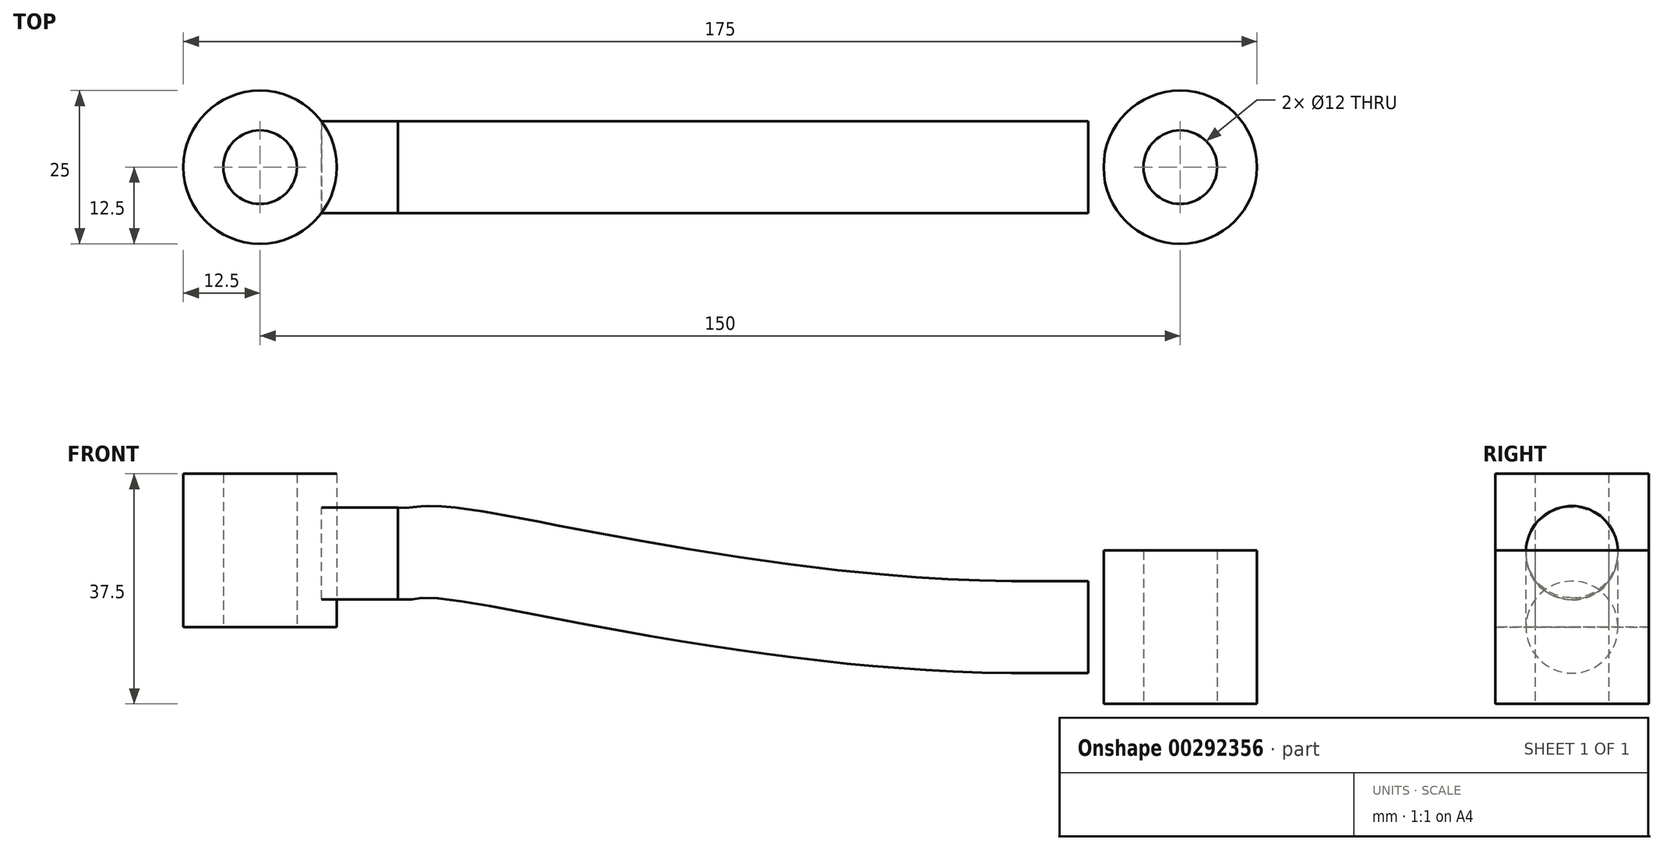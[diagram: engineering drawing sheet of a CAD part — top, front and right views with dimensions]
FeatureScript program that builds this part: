
annotation { "Feature Type Name" : "Feature", "Feature Type Description" : "" }
export const myFeature = defineFeature(function(context is Context, id is Id, definition is map)
    precondition{}
    {
        {
            var Q0;
            Q0=qCreatedBy(makeId("Top.planeOp"),FACE);
            var sketch = newSketch(context, id + "F0", { "sketchPlane" : qUnion([Q0])});
            skCircle(sketch, "E0", {"center": v(0, 0) * mm, "radius": 12.5 * mm});
            skCircle(sketch, "E1", {"center": v(0, 0) * mm, "radius": 6 * mm});
            skSolve(sketch);
        }
        {
            var Q0;
            Q0=makeQuery(id+"F0.imprint","IMPRINT",FACE,{"disambiguationData":[TD([[makeQuery(id+"F0.imprint","IMPRINT",EDGE,{"derivedFrom":sQuery(id+"F0.wireOp",EDGE,"E0")}),1.0]])]});
            extrude(context, id + "F1", {"entities" : qUnion([Q0]), "depth" : 25 * mm});
        }
        {
            var Q0;
            Q0=qCreatedBy(makeId("Top.planeOp"),FACE);
            var sketch = newSketch(context, id + "F2", { "sketchPlane" : qUnion([Q0])});
            skCircle(sketch, "E2", {"center": v(150, 0) * mm, "radius": 12.5 * mm});
            skCircle(sketch, "E3", {"center": v(150, 0) * mm, "radius": 6 * mm});
            skSolve(sketch);
        }
        {
            var Q0;
            Q0=makeQuery(id+"F2.imprint","IMPRINT",FACE,{"disambiguationData":[TD([[makeQuery(id+"F2.imprint","IMPRINT",EDGE,{"derivedFrom":sQuery(id+"F2.wireOp",EDGE,"E2")}),1.0]])]});
            extrude(context, id + "F3", {"entities" : qUnion([Q0]), "endBound" : BoundingType.SYMMETRIC, "depth" : 25 * mm});
        }
        {
            var Q0;
            Q0=qCreatedBy(makeId("Front.planeOp"),FACE);
            var sketch = newSketch(context, id + "F4", { "sketchPlane" : qUnion([Q0])});
            skLineSegment(sketch, "E4", {"start": v(12.5, 25) * mm, "end": v(12.5, 0.03) * mm});
            skLineSegment(sketch, "E5", {"start": v(137.5, -12.5) * mm, "end": v(137.5, 12.5) * mm});
            skLineSegment(sketch, "E6", {"start": v(12.5, 12.03) * mm, "end": v(25, 12.03) * mm});
            skLineSegment(sketch, "E7", {"start": v(137.5, 0) * mm, "end": v(125, 0) * mm});
            skPoint(sketch, "E7.endSnap0", {"position": v(137.5, 0) * mm});
            skFitSpline(sketch, "E8", {"points": [v(25, 12.03) * mm, v(30.75, 12.03) * mm, v(125, 0) * mm], "startDerivative": vector(20.63, 0) * mm, "endDerivative": vector(153.84, 0) * mm});
            skSolve(sketch);
        }
        {
            var Q0;
            Q0=qCreatedBy(makeId("Right.planeOp"),FACE);
            cPlane(context, id + "F5", {"entities" : qUnion([Q0]), "cplaneType" : CPlaneType.OFFSET, "offset" : 10 * mm, "width" : 150 * mm, "height" : 150 * mm});
        }
        {
            var Q0;
            Q0=qCreatedBy(id+"F5.planeOp",FACE);
            var sketch = newSketch(context, id + "F6", { "sketchPlane" : qUnion([Q0])});
            skCircle(sketch, "E9", {"center": v(0, 12.03) * mm, "radius": 7.5 * mm});
            skSolve(sketch);
        }
        {
            var Q0;
            Q0 = qSketchRegion(id + "F6", true);
            var Q1;
            Q1=sQuery(id+"F4.wireOp",EDGE,"E6");
            var Q2;
            Q2=sQuery(id+"F4.wireOp",EDGE,"E8");
            var Q3;
            Q3=sQuery(id+"F4.wireOp",EDGE,"E7");
            sweep(context, id + "F7", {"profiles" : qUnion([Q0]), "path" : qUnion([Q1, Q2, Q3])});
        }
    });
